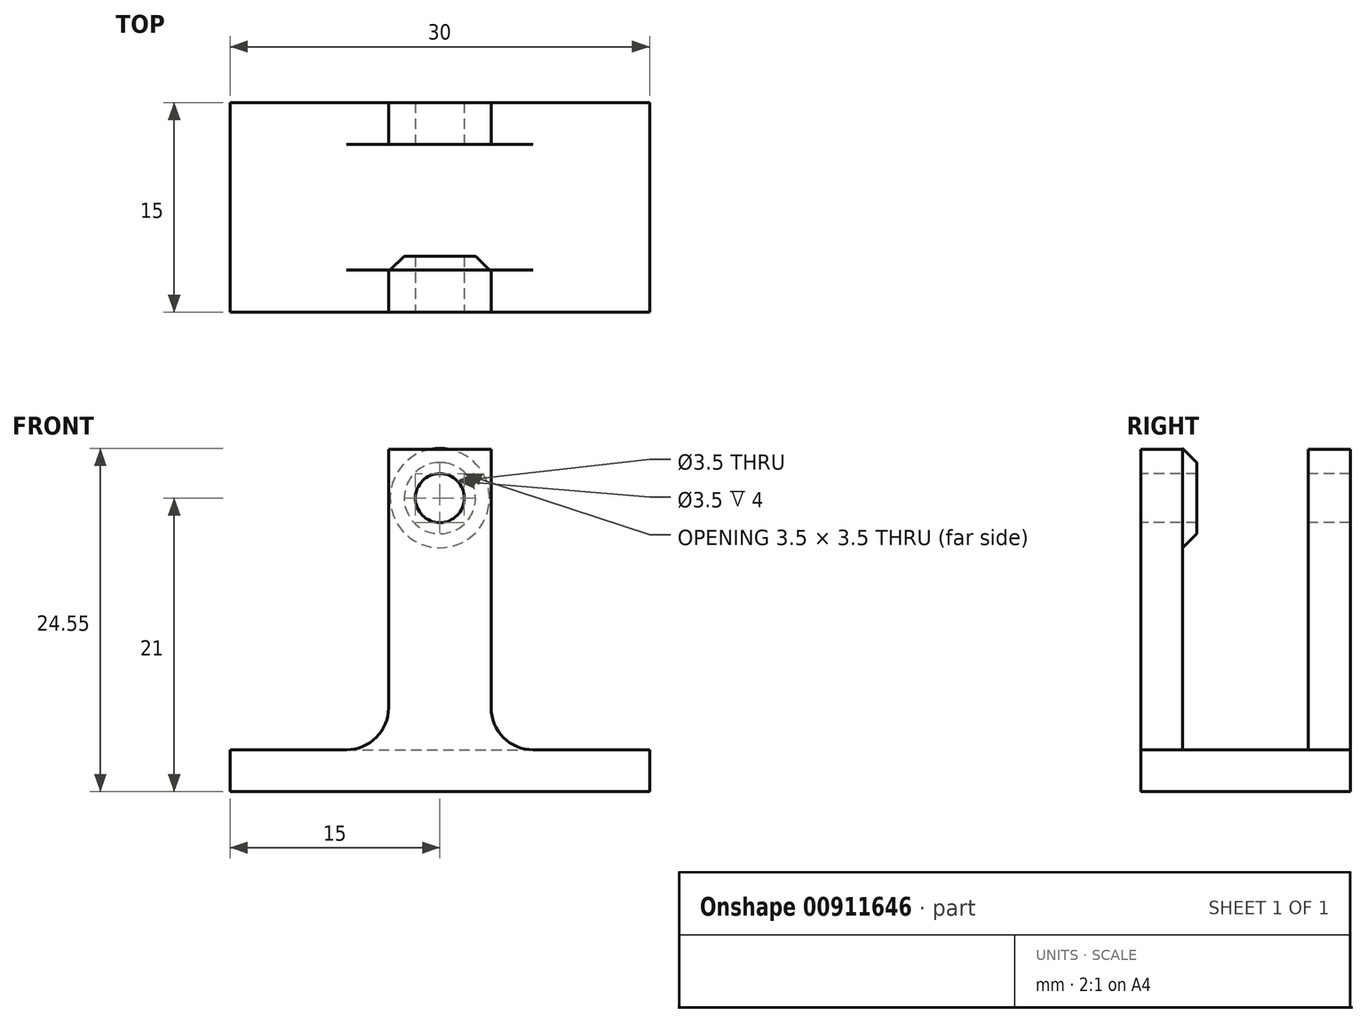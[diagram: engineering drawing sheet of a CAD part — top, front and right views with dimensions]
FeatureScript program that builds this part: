
annotation { "Feature Type Name" : "Feature", "Feature Type Description" : "" }
export const myFeature = defineFeature(function(context is Context, id is Id, definition is map)
    precondition{}
    {
        {
            var Q0;
            Q0=qCreatedBy(makeId("Top.planeOp"),FACE);
            var sketch = newSketch(context, id + "F0", { "sketchPlane" : qUnion([Q0])});
            skLineSegment(sketch, "E0.bottom", {"start": v(-15, -7.5) * mm, "end": v(15, -7.5) * mm});
            skLineSegment(sketch, "E0.top", {"start": v(-15, 7.5) * mm, "end": v(15, 7.5) * mm});
            skLineSegment(sketch, "E0.left", {"start": v(-15, -7.5) * mm, "end": v(-15, 7.5) * mm});
            skLineSegment(sketch, "E0.right", {"start": v(15, -7.5) * mm, "end": v(15, 7.5) * mm});
            skPoint(sketch, "E0.middle", {"position": v(0, 0) * mm});
            skSolve(sketch);
        }
        {
            var Q0;
            Q0 = qSketchRegion(id + "F0", true);
            extrude(context, id + "F1", {"entities" : qUnion([Q0]), "depth" : 3 * mm, "offsetDistance" : 25 * mm});
        }
        {
            var Q0;
            Q0=makeQuery(id+"F1.opExtrude","CAP_FACE",FACE,{"disambiguationData":[OSD([sQuery(id+"F0.wireOp",EDGE,"E0.bottom"),sQuery(id+"F0.wireOp",EDGE,"E0.top"),sQuery(id+"F0.wireOp",EDGE,"E0.left"),sQuery(id+"F0.wireOp",EDGE,"E0.right")])],"isStart":false});
            var sketch = newSketch(context, id + "F2", { "sketchPlane" : qUnion([Q0])});
            skLineSegment(sketch, "E1.bottom", {"start": v(-15, -7.5) * mm, "end": v(15, -7.5) * mm});
            skLineSegment(sketch, "E1.top", {"start": v(-15, -4.5) * mm, "end": v(15, -4.5) * mm});
            skLineSegment(sketch, "E1.left", {"start": v(-15, -7.5) * mm, "end": v(-15, -4.5) * mm});
            skLineSegment(sketch, "E1.right", {"start": v(15, -7.5) * mm, "end": v(15, -4.5) * mm});
            skLineSegment(sketch, "E2.bottom", {"start": v(15, 7.5) * mm, "end": v(-15, 7.5) * mm});
            skLineSegment(sketch, "E2.top", {"start": v(15, 4.5) * mm, "end": v(-15, 4.5) * mm});
            skLineSegment(sketch, "E2.left", {"start": v(15, 7.5) * mm, "end": v(15, 4.5) * mm});
            skLineSegment(sketch, "E2.right", {"start": v(-15, 7.5) * mm, "end": v(-15, 4.5) * mm});
            skSolve(sketch);
        }
        {
            var Q0;
            Q0 = qSketchRegion(id + "F2", true);
            extrude(context, id + "F3", {"entities" : qUnion([Q0]), "operationType" : NewBodyOperationType.ADD, "depth" : 21.5 * mm, "offsetDistance" : 25 * mm});
        }
        {
            var Q0;
            Q0=makeQuery(id+"F3.boolean.opBoolean","MERGE",FACE,{"derivedFrom":[makeQuery(id+"F1.opExtrude","SWEPT_FACE",FACE,{"disambiguationData":[OSD([sQuery(id+"F0.wireOp",EDGE,"E0.bottom")])]}),makeQuery(id+"F3.opExtrude","SWEPT_FACE",FACE,{"disambiguationData":[OSD([sQuery(id+"F2.wireOp",EDGE,"E1.bottom")])]})]});
            var sketch = newSketch(context, id + "F4", { "sketchPlane" : qUnion([Q0])});
            skCircle(sketch, "E3", {"center": v(0, 21) * mm, "radius": 1.75 * mm});
            skLineSegment(sketch, "E4", {"start": v(-3.67, 24.5) * mm, "end": v(-3.67, 3) * mm});
            skLineSegment(sketch, "E5", {"start": v(3.67, 24.5) * mm, "end": v(3.67, 3) * mm});
            skLineSegment(sketch, "E6", {"start": v(-15, 24.5) * mm, "end": v(-3.67, 24.5) * mm});
            skLineSegment(sketch, "E7", {"start": v(3.67, 24.5) * mm, "end": v(15, 24.5) * mm});
            skLineSegment(sketch, "E8", {"start": v(-15, 24.5) * mm, "end": v(-15, 0) * mm});
            skLineSegment(sketch, "E9", {"start": v(-15, 0) * mm, "end": v(-3.67, 0) * mm});
            skLineSegment(sketch, "E10", {"start": v(3.67, 0) * mm, "end": v(15, 0) * mm});
            skLineSegment(sketch, "E11", {"start": v(15, 0) * mm, "end": v(15, 24.5) * mm});
            skLineSegment(sketch, "E12", {"start": v(-15, 3) * mm, "end": v(15, 3) * mm});
            skSolve(sketch);
        }
        {
            var Q0;
            Q0 = qSketchRegion(id + "F4", true);
            extrude(context, id + "F5", {"entities" : qUnion([Q0]), "operationType" : NewBodyOperationType.REMOVE, "endBound" : BoundingType.THROUGH_ALL, "oppositeDirection" : true, "depth" : 25 * mm, "offsetDistance" : 25 * mm});
        }
        {
            var Q0;
            {var subQ0=sQuery(id+"F4.wireOp",EDGE,"E12");var subQ1=sQuery(id+"F4.wireOp",EDGE,"E4");var subQ2=sQuery(id+"F0.wireOp",EDGE,"E0.bottom");Q0=makeQuery(id+"F5.boolean.opBoolean","COPY",EDGE,{"disambiguationData":[TD([makeQuery(id+"F1.opExtrude","SWEPT_FACE",FACE,{"disambiguationData":[OSD([subQ2])]})])],"derivedFrom":makeQuery(id+"F5.opExtrude","SWEPT_EDGE",EDGE,{"disambiguationData":[OSD([subQ1,subQ0])]})});}
            var Q1;
            {var subQ0=sQuery(id+"F0.wireOp",EDGE,"E0.top");var subQ1=sQuery(id+"F4.wireOp",EDGE,"E4");var subQ2=sQuery(id+"F4.wireOp",EDGE,"E12");Q1=makeQuery(id+"F5.boolean.opBoolean","COPY",EDGE,{"disambiguationData":[TD([makeQuery(id+"F1.opExtrude","SWEPT_FACE",FACE,{"disambiguationData":[OSD([subQ0])]})])],"derivedFrom":makeQuery(id+"F5.opExtrude","SWEPT_EDGE",EDGE,{"disambiguationData":[OSD([subQ1,subQ2])]})});}
            var Q2;
            {var subQ0=sQuery(id+"F4.wireOp",EDGE,"E12");var subQ1=sQuery(id+"F0.wireOp",EDGE,"E0.bottom");var subQ2=sQuery(id+"F4.wireOp",EDGE,"E5");Q2=makeQuery(id+"F5.boolean.opBoolean","COPY",EDGE,{"disambiguationData":[TD([makeQuery(id+"F1.opExtrude","SWEPT_FACE",FACE,{"disambiguationData":[OSD([subQ1])]})])],"derivedFrom":makeQuery(id+"F5.opExtrude","SWEPT_EDGE",EDGE,{"disambiguationData":[OSD([subQ2,subQ0])]})});}
            var Q3;
            {var subQ0=sQuery(id+"F0.wireOp",EDGE,"E0.top");var subQ1=sQuery(id+"F4.wireOp",EDGE,"E12");var subQ2=sQuery(id+"F4.wireOp",EDGE,"E5");Q3=makeQuery(id+"F5.boolean.opBoolean","COPY",EDGE,{"disambiguationData":[TD([makeQuery(id+"F1.opExtrude","SWEPT_FACE",FACE,{"disambiguationData":[OSD([subQ0])]})])],"derivedFrom":makeQuery(id+"F5.opExtrude","SWEPT_EDGE",EDGE,{"disambiguationData":[OSD([subQ2,subQ1])]})});}
            var Q4;
            {var subQ0=sQuery(id+"F2.wireOp",EDGE,"E1.bottom");var subQ1=sQuery(id+"F4.wireOp",EDGE,"E5");Q4=makeQuery(id+"F5.boolean.opBoolean","COPY",EDGE,{"disambiguationData":[topologyDisambiguationEdgeConnected([makeQuery(id+"F3.opExtrude","CAP_FACE",FACE,{"disambiguationData":[OSD([subQ0,sQuery(id+"F2.wireOp",EDGE,"E1.top"),sQuery(id+"F2.wireOp",EDGE,"E1.left"),sQuery(id+"F2.wireOp",EDGE,"E1.right")])],"isStart":false})])],"derivedFrom":makeQuery(id+"F5.opExtrude","SWEPT_EDGE",EDGE,{"disambiguationData":[OSD([subQ0,subQ1,sQuery(id+"F4.wireOp",EDGE,"E7")])]})});}
            var Q5;
            {var subQ0=sQuery(id+"F2.wireOp",EDGE,"E1.bottom");var subQ1=sQuery(id+"F4.wireOp",EDGE,"E4");Q5=makeQuery(id+"F5.boolean.opBoolean","COPY",EDGE,{"disambiguationData":[topologyDisambiguationEdgeConnected([makeQuery(id+"F3.opExtrude","CAP_FACE",FACE,{"disambiguationData":[OSD([subQ0,sQuery(id+"F2.wireOp",EDGE,"E1.top"),sQuery(id+"F2.wireOp",EDGE,"E1.left"),sQuery(id+"F2.wireOp",EDGE,"E1.right")])],"isStart":false})])],"derivedFrom":makeQuery(id+"F5.opExtrude","SWEPT_EDGE",EDGE,{"disambiguationData":[OSD([subQ0,subQ1,sQuery(id+"F4.wireOp",EDGE,"E6")])]})});}
            var Q6;
            {var subQ0=sQuery(id+"F4.wireOp",EDGE,"E4");Q6=makeQuery(id+"F5.boolean.opBoolean","COPY",EDGE,{"disambiguationData":[topologyDisambiguationEdgeConnected([makeQuery(id+"F3.opExtrude","CAP_FACE",FACE,{"disambiguationData":[OSD([sQuery(id+"F2.wireOp",EDGE,"E2.bottom"),sQuery(id+"F2.wireOp",EDGE,"E2.top"),sQuery(id+"F2.wireOp",EDGE,"E2.left"),sQuery(id+"F2.wireOp",EDGE,"E2.right")])],"isStart":false})])],"derivedFrom":makeQuery(id+"F5.opExtrude","SWEPT_EDGE",EDGE,{"disambiguationData":[OSD([sQuery(id+"F2.wireOp",EDGE,"E1.bottom"),subQ0,sQuery(id+"F4.wireOp",EDGE,"E6")])]})});}
            var Q7;
            {var subQ0=sQuery(id+"F4.wireOp",EDGE,"E5");Q7=makeQuery(id+"F5.boolean.opBoolean","COPY",EDGE,{"disambiguationData":[topologyDisambiguationEdgeConnected([makeQuery(id+"F3.opExtrude","CAP_FACE",FACE,{"disambiguationData":[OSD([sQuery(id+"F2.wireOp",EDGE,"E2.bottom"),sQuery(id+"F2.wireOp",EDGE,"E2.top"),sQuery(id+"F2.wireOp",EDGE,"E2.left"),sQuery(id+"F2.wireOp",EDGE,"E2.right")])],"isStart":false})])],"derivedFrom":makeQuery(id+"F5.opExtrude","SWEPT_EDGE",EDGE,{"disambiguationData":[OSD([sQuery(id+"F2.wireOp",EDGE,"E1.bottom"),subQ0,sQuery(id+"F4.wireOp",EDGE,"E7")])]})});}
            var Q8;
            Q8=makeQuery(id+"F5.boolean.opBoolean","MERGE",EDGE,{"derivedFrom":[makeQuery(id+"F1.opExtrude","CAP_EDGE",EDGE,{"disambiguationData":[OSD([sQuery(id+"F0.wireOp",EDGE,"E0.left")])],"isStart":false})],"fromTools":[makeQuery(id+"F5.opExtrude","SWEPT_EDGE",EDGE,{"disambiguationData":[OSD([sQuery(id+"F4.wireOp",EDGE,"E8"),sQuery(id+"F4.wireOp",EDGE,"E12")])]})]});
            var Q9;
            Q9=makeQuery(id+"F5.boolean.opBoolean","MERGE",EDGE,{"derivedFrom":[makeQuery(id+"F1.opExtrude","CAP_EDGE",EDGE,{"disambiguationData":[OSD([sQuery(id+"F0.wireOp",EDGE,"E0.right")])],"isStart":false})],"fromTools":[makeQuery(id+"F5.opExtrude","SWEPT_EDGE",EDGE,{"disambiguationData":[OSD([sQuery(id+"F4.wireOp",EDGE,"E11"),sQuery(id+"F4.wireOp",EDGE,"E12")])]})]});
            fillet(context, id + "F6", {"entities" : qUnion([Q0, Q1, Q2, Q3, Q4, Q5, Q6, Q7, Q8, Q9]), "radius" : 3 * mm, "tangentPropagation" : true, "allowEdgeOverflow" : false});
        }
        {
            var Q0;
            Q0=makeQuery(id+"F3.opExtrude","SWEPT_FACE",FACE,{"disambiguationData":[OSD([sQuery(id+"F2.wireOp",EDGE,"E1.top")])]});
            var sketch = newSketch(context, id + "F7", { "sketchPlane" : qUnion([Q0])});
            skCircle(sketch, "E13", {"center": v(0, 21) * mm, "radius": 3.55 * mm});
            skCircle(sketch, "E14", {"center": v(0, 21) * mm, "radius": 1.75 * mm});
            skSolve(sketch);
        }
        {
            var Q0;
            Q0 = qSketchRegion(id + "F7", true);
            extrude(context, id + "F8", {"entities" : qUnion([Q0]), "operationType" : NewBodyOperationType.ADD, "depth" : 1 * mm, "offsetDistance" : 25 * mm});
        }
        {
            var Q0;
            Q0=makeQuery(id+"F8.opExtrude","CAP_EDGE",EDGE,{"disambiguationData":[OSD([sQuery(id+"F7.wireOp",EDGE,"E13")])],"isStart":false});
            chamfer(context, id + "F9", {"entities" : qUnion([Q0]), "width" : 1 * mm, "tangentPropagation" : true});
        }
    });
